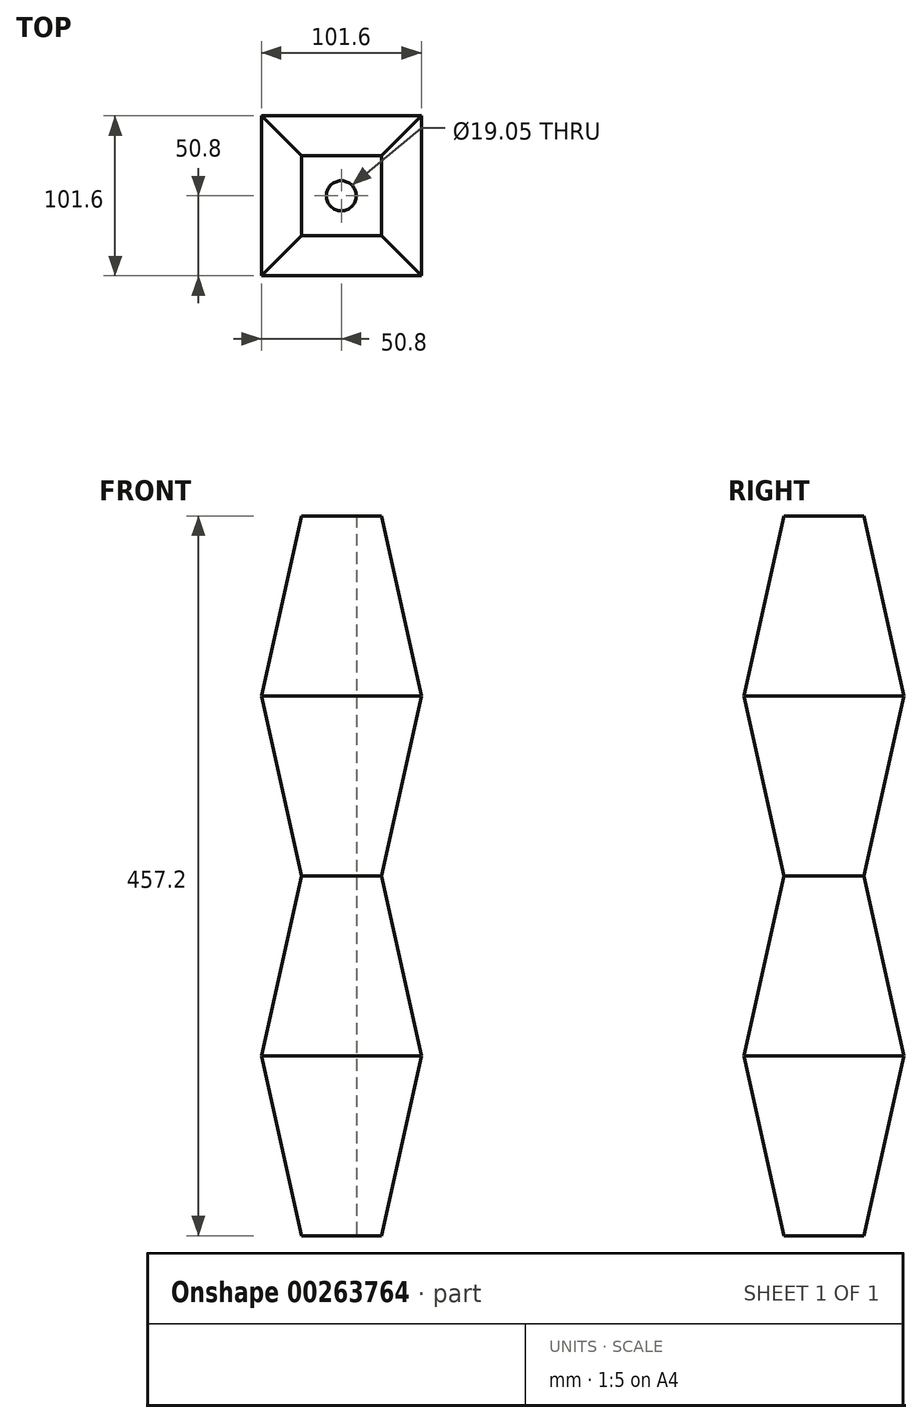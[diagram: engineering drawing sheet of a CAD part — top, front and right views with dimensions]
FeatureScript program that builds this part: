
annotation { "Feature Type Name" : "Feature", "Feature Type Description" : "" }
export const myFeature = defineFeature(function(context is Context, id is Id, definition is map)
    precondition{}
    {
        {
            var Q0;
            Q0=qCreatedBy(makeId("Top.planeOp"),FACE);
            var sketch = newSketch(context, id + "F0", { "sketchPlane" : qUnion([Q0])});
            skLineSegment(sketch, "E0.bottom", {"start": v(50.8, -50.8) * mm, "end": v(-50.8, -50.8) * mm});
            skLineSegment(sketch, "E0.top", {"start": v(50.8, 50.8) * mm, "end": v(-50.8, 50.8) * mm});
            skLineSegment(sketch, "E0.left", {"start": v(50.8, -50.8) * mm, "end": v(50.8, 50.8) * mm});
            skLineSegment(sketch, "E0.right", {"start": v(-50.8, -50.8) * mm, "end": v(-50.8, 50.8) * mm});
            skPoint(sketch, "E0.middle", {"position": v(0, 0) * mm});
            skSolve(sketch);
        }
        {
            var Q0;
            Q0=makeQuery(id+"F0.imprint","IMPRINT",FACE,{"disambiguationData":[TD([[makeQuery(id+"F0.imprint","IMPRINT",EDGE,{"derivedFrom":sQuery(id+"F0.wireOp",EDGE,"E0.bottom")}),-1.0]])]});
            extrude(context, id + "F1", {"entities" : qUnion([Q0]), "depth" : 457.2 * mm});
        }
        {
            var Q0;
            Q0=qCreatedBy(makeId("Front.planeOp"),FACE);
            var sketch = newSketch(context, id + "F2", { "sketchPlane" : qUnion([Q0])});
            skLineSegment(sketch, "E1.0.0", {"start": v(-50.8, 0) * mm, "end": v(-25.4, 0) * mm});
            skLineSegment(sketch, "E1.0.2", {"start": v(50.8, 457.2) * mm, "end": v(25.4, 457.2) * mm});
            skLineSegment(sketch, "E2", {"start": v(25.4, 457.2) * mm, "end": v(50.8, 342.9) * mm});
            skLineSegment(sketch, "E3", {"start": v(-25.4, 457.2) * mm, "end": v(-50.8, 342.9) * mm});
            skLineSegment(sketch, "E4", {"start": v(-50.8, 114.3) * mm, "end": v(-25.4, 0) * mm});
            skLineSegment(sketch, "E5", {"start": v(50.8, 114.3) * mm, "end": v(25.4, 0) * mm});
            skLineSegment(sketch, "E6.trimOffspring", {"start": v(-25.4, 457.2) * mm, "end": v(-50.8, 457.2) * mm});
            skLineSegment(sketch, "E7.trimOffspring", {"start": v(25.4, 0) * mm, "end": v(50.8, 0) * mm});
            skLineSegment(sketch, "E8", {"start": v(-50.8, 342.9) * mm, "end": v(-25.4, 228.6) * mm});
            skLineSegment(sketch, "E9", {"start": v(-25.4, 228.6) * mm, "end": v(-50.8, 114.3) * mm});
            skLineSegment(sketch, "E10", {"start": v(50.8, 342.9) * mm, "end": v(25.4, 228.6) * mm});
            skLineSegment(sketch, "E11", {"start": v(25.4, 228.6) * mm, "end": v(50.8, 114.3) * mm});
            skLineSegment(sketch, "E12", {"start": v(-50.8, 457.2) * mm, "end": v(-76.2, 457.2) * mm});
            skLineSegment(sketch, "E13", {"start": v(-76.2, 457.2) * mm, "end": v(-76.2, 0) * mm});
            skLineSegment(sketch, "E14", {"start": v(-76.2, 0) * mm, "end": v(-50.8, 0) * mm});
            skLineSegment(sketch, "E15", {"start": v(50.8, 457.2) * mm, "end": v(76.2, 457.2) * mm});
            skLineSegment(sketch, "E16", {"start": v(76.2, 457.2) * mm, "end": v(76.2, 0) * mm});
            skLineSegment(sketch, "E17", {"start": v(76.2, 0) * mm, "end": v(50.8, 0) * mm});
            skSolve(sketch);
        }
        {
            var Q0;
            Q0 = qSketchRegion(id + "F2", true);
            extrude(context, id + "F3", {"entities" : qUnion([Q0]), "operationType" : NewBodyOperationType.REMOVE, "endBound" : BoundingType.THROUGH_ALL, "oppositeDirection" : true, "depth" : 25.4 * mm, "hasSecondDirection" : true, "secondDirectionBound" : SecondDirectionBoundingType.THROUGH_ALL, "secondDirectionOppositeDirection" : false, "secondDirectionDepth" : 25.4 * mm});
        }
        {
            var Q0;
            Q0=qCreatedBy(makeId("Right.planeOp"),FACE);
            var sketch = newSketch(context, id + "F4", { "sketchPlane" : qUnion([Q0])});
            skLineSegment(sketch, "E18.0", {"start": v(50.8, 457.2) * mm, "end": v(25.4, 457.2) * mm});
            skLineSegment(sketch, "E19", {"start": v(25.4, 457.2) * mm, "end": v(50.8, 342.9) * mm});
            skLineSegment(sketch, "E20", {"start": v(50.8, 342.9) * mm, "end": v(25.4, 228.6) * mm});
            skLineSegment(sketch, "E21", {"start": v(25.4, 228.6) * mm, "end": v(50.8, 114.3) * mm});
            skLineSegment(sketch, "E22", {"start": v(50.8, 114.3) * mm, "end": v(25.4, 0) * mm});
            skLineSegment(sketch, "E23", {"start": v(25.4, 0) * mm, "end": v(50.8, 0) * mm});
            skLineSegment(sketch, "E24", {"start": v(76.2, 0) * mm, "end": v(76.2, 457.2) * mm});
            skLineSegment(sketch, "E25", {"start": v(76.2, 457.2) * mm, "end": v(50.8, 457.2) * mm});
            skLineSegment(sketch, "E26", {"start": v(76.2, 0) * mm, "end": v(50.8, 0) * mm});
            skLineSegment(sketch, "E27", {"start": v(-50.8, 457.2) * mm, "end": v(-76.2, 457.2) * mm});
            skLineSegment(sketch, "E28", {"start": v(-76.2, 457.2) * mm, "end": v(-76.2, 0) * mm});
            skLineSegment(sketch, "E29", {"start": v(-76.2, 0) * mm, "end": v(-50.8, 0) * mm});
            skLineSegment(sketch, "E30", {"start": v(-25.4, 457.2) * mm, "end": v(-50.8, 342.9) * mm});
            skLineSegment(sketch, "E31", {"start": v(-50.8, 342.9) * mm, "end": v(-25.4, 228.6) * mm});
            skLineSegment(sketch, "E32", {"start": v(-25.4, 228.6) * mm, "end": v(-50.8, 114.3) * mm});
            skLineSegment(sketch, "E33", {"start": v(-50.8, 114.3) * mm, "end": v(-25.4, 0) * mm});
            skLineSegment(sketch, "E34", {"start": v(-25.4, 0) * mm, "end": v(-50.8, 0) * mm});
            skLineSegment(sketch, "E35.trimOffspring", {"start": v(-25.4, 457.2) * mm, "end": v(-50.8, 457.2) * mm});
            skPoint(sketch, "E36.0.start.orphan", {"position": v(-50.8, 228.6) * mm});
            skPoint(sketch, "E37.0.end.orphan", {"position": v(50.8, 228.6) * mm});
            skSolve(sketch);
        }
        {
            var Q0;
            Q0 = qSketchRegion(id + "F4", true);
            extrude(context, id + "F5", {"entities" : qUnion([Q0]), "operationType" : NewBodyOperationType.REMOVE, "endBound" : BoundingType.THROUGH_ALL, "oppositeDirection" : true, "depth" : 25.4 * mm, "hasSecondDirection" : true, "secondDirectionBound" : SecondDirectionBoundingType.THROUGH_ALL, "secondDirectionOppositeDirection" : false, "secondDirectionDepth" : 25.4 * mm});
        }
        {
            var Q0;
            Q0=qCreatedBy(makeId("Top.planeOp"),FACE);
            var sketch = newSketch(context, id + "F6", { "sketchPlane" : qUnion([Q0])});
            skCircle(sketch, "E38", {"center": v(0, 0) * mm, "radius": 9.53 * mm});
            skSolve(sketch);
        }
        {
            var Q0;
            Q0=makeQuery(id+"F6.imprint","IMPRINT",FACE,{"disambiguationData":[TD([[makeQuery(id+"F6.imprint","IMPRINT",EDGE,{"derivedFrom":sQuery(id+"F6.wireOp",EDGE,"E38")}),1.0]])]});
            extrude(context, id + "F7", {"entities" : qUnion([Q0]), "operationType" : NewBodyOperationType.REMOVE, "endBound" : BoundingType.THROUGH_ALL, "depth" : 25.4 * mm, "hasSecondDirection" : true, "secondDirectionBound" : SecondDirectionBoundingType.THROUGH_ALL, "secondDirectionOppositeDirection" : true, "secondDirectionDepth" : 25.4 * mm});
        }
    });
